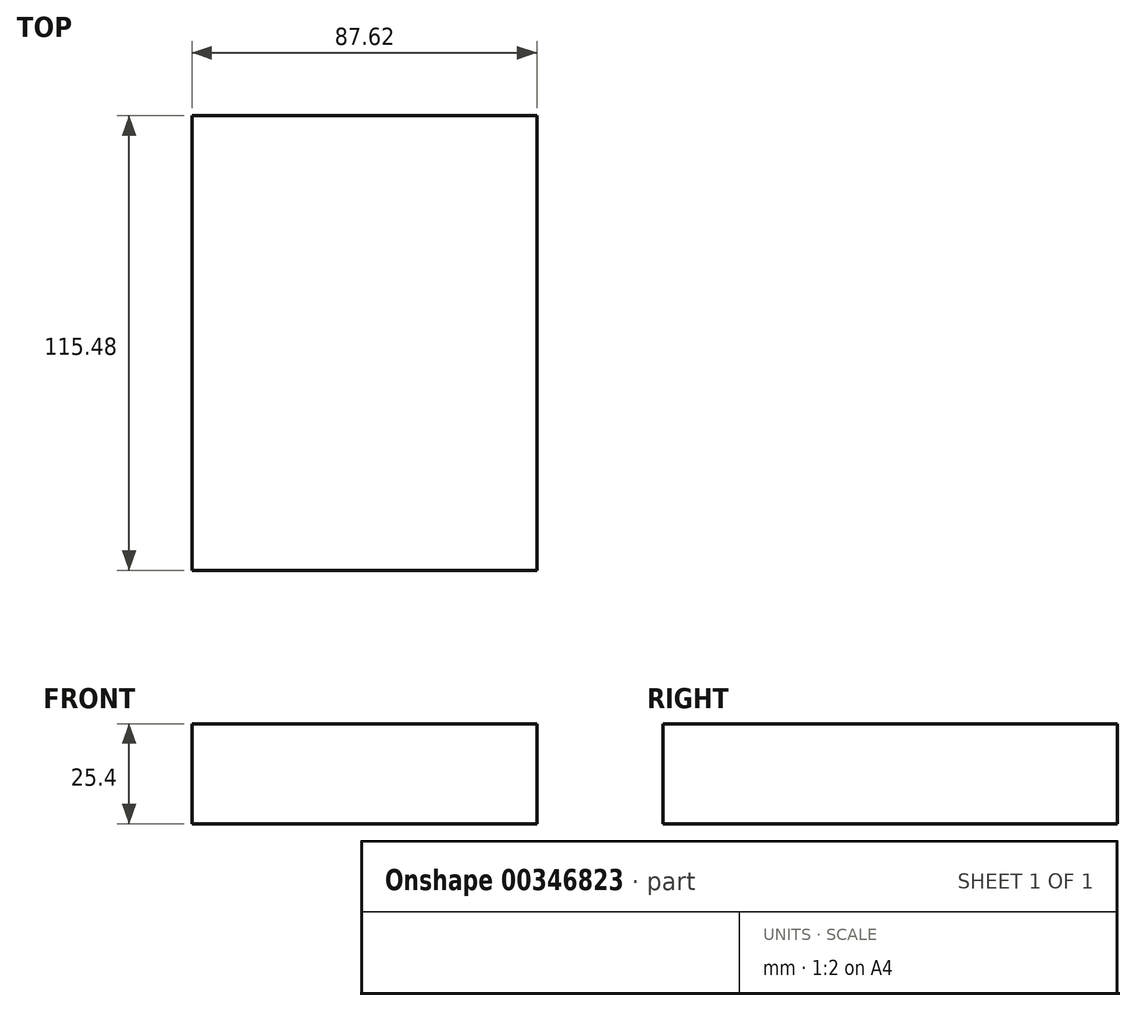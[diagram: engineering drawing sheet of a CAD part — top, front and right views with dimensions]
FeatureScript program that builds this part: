
annotation { "Feature Type Name" : "Feature", "Feature Type Description" : "" }
export const myFeature = defineFeature(function(context is Context, id is Id, definition is map)
    precondition{}
    {
        {
            var Q0;
            Q0=qCreatedBy(makeId("Top.planeOp"),FACE);
            var sketch = newSketch(context, id + "F0", { "sketchPlane" : qUnion([Q0])});
            skLineSegment(sketch, "E0.bottom", {"start": v(0, 0) * mm, "end": v(87.62, 0) * mm});
            skLineSegment(sketch, "E0.top", {"start": v(0, 115.48) * mm, "end": v(87.62, 115.48) * mm});
            skLineSegment(sketch, "E0.left", {"start": v(0, 0) * mm, "end": v(0, 115.48) * mm});
            skLineSegment(sketch, "E0.right", {"start": v(87.62, 0) * mm, "end": v(87.62, 115.48) * mm});
            skPoint(sketch, "E0.middle", {"position": v(43.81, 57.74) * mm});
            skSolve(sketch);
        }
        {
            var Q0;
            Q0=makeQuery(id+"F0.imprint","IMPRINT",FACE,{"disambiguationData":[TD([[makeQuery(id+"F0.imprint","IMPRINT",EDGE,{"derivedFrom":sQuery(id+"F0.wireOp",EDGE,"E0.bottom")}),1.0]])]});
            var sketch = newSketch(context, id + "F1", { "sketchPlane" : qUnion([Q0])});
            skSolve(sketch);
        }
        {
            var Q0;
            Q0 = qSketchRegion(id + "F1", true);
            var Q1;
            Q1=makeQuery(id+"F0.imprint","IMPRINT",FACE,{"disambiguationData":[TD([[makeQuery(id+"F0.imprint","IMPRINT",EDGE,{"derivedFrom":sQuery(id+"F0.wireOp",EDGE,"E0.bottom")}),1.0]])]});
            extrude(context, id + "F2", {"entities" : qUnion([Q0, Q1]), "depth" : 25.4 * mm});
        }
    });
